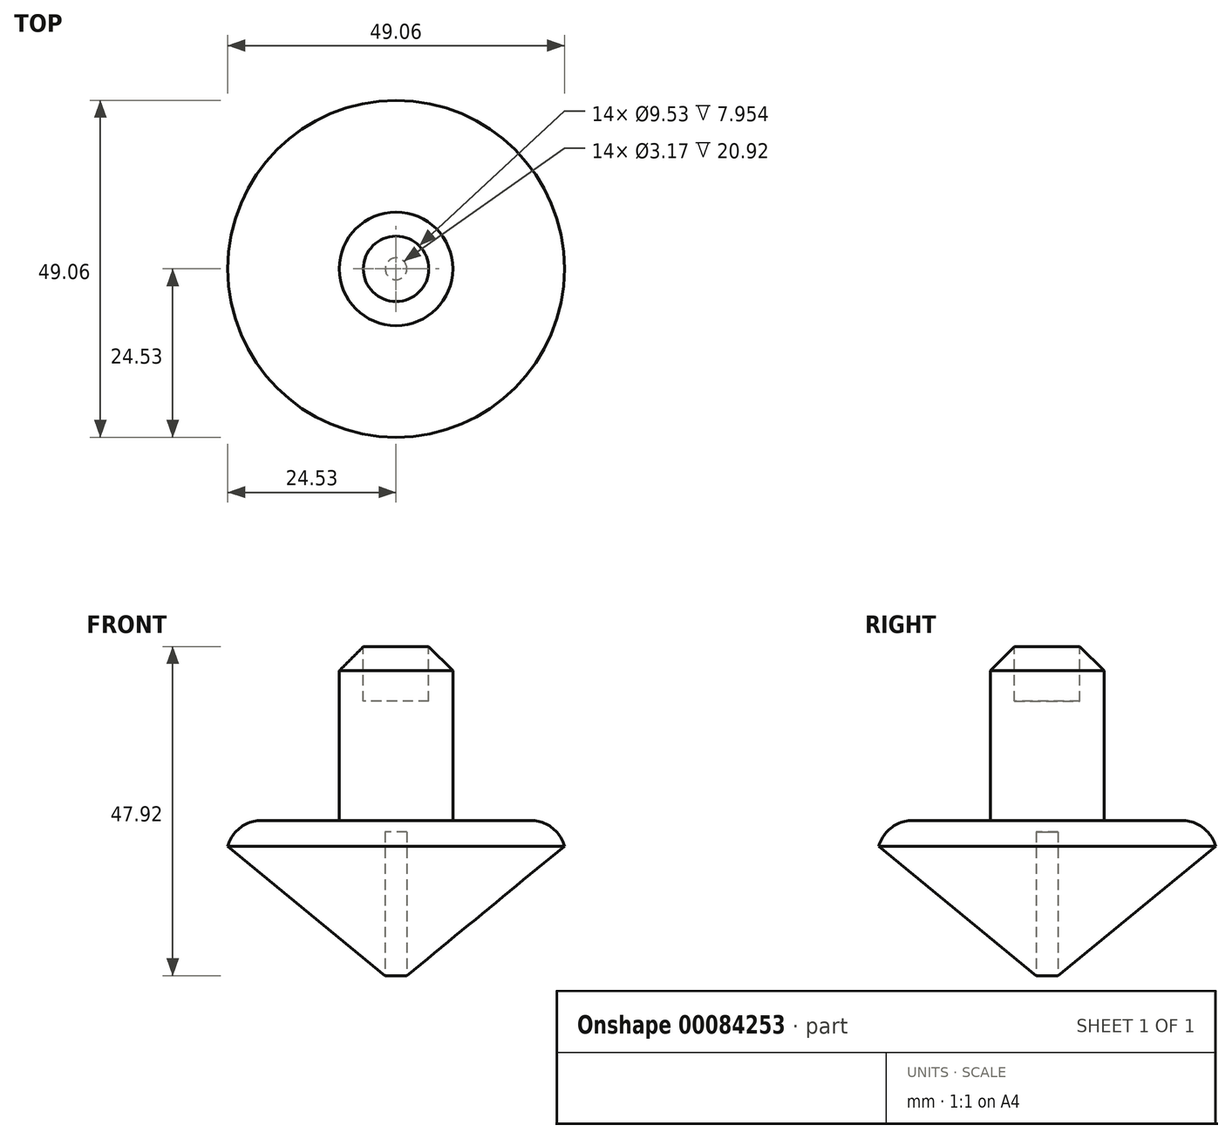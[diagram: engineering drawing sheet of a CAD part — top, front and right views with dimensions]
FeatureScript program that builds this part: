
annotation { "Feature Type Name" : "Feature", "Feature Type Description" : "" }
export const myFeature = defineFeature(function(context is Context, id is Id, definition is map)
    precondition{}
    {
        {
            var Q0;
            Q0=qCreatedBy(makeId("Front.planeOp"),FACE);
            var sketch = newSketch(context, id + "F0", { "sketchPlane" : qUnion([Q0])});
            skLineSegment(sketch, "E0", {"start": v(0, 0) * mm, "end": v(24.53, 20.16) * mm});
            skLineSegment(sketch, "E1", {"start": v(24.53, 20.16) * mm, "end": v(24.53, 23.9) * mm});
            skLineSegment(sketch, "E2", {"start": v(24.53, 23.9) * mm, "end": v(8.27, 23.9) * mm});
            skLineSegment(sketch, "E3", {"start": v(8.27, 23.9) * mm, "end": v(8.27, 50.8) * mm});
            skLineSegment(sketch, "E4", {"start": v(8.27, 50.8) * mm, "end": v(0, 50.8) * mm});
            skLineSegment(sketch, "E5", {"start": v(0, 50.8) * mm, "end": v(0, 0) * mm});
            skSolve(sketch);
        }
        {
            var Q0;
            Q0=qCreatedBy(makeId("Front.planeOp"),FACE);
            var sketch = newSketch(context, id + "F1", { "sketchPlane" : qUnion([Q0])});
            skSolve(sketch);
        }
        {
            var Q0;
            Q0 = qSketchRegion(id + "F1", true);
            var Q1;
            Q1=makeQuery(id+"F0.imprint","IMPRINT",FACE,{"disambiguationData":[TD([[makeQuery(id+"F0.imprint","IMPRINT",EDGE,{"derivedFrom":sQuery(id+"F0.wireOp",EDGE,"E0")}),1.0]])]});
            var Q2;
            Q2=sQuery(id+"F0.wireOp",EDGE,"E5");
            revolve(context, id + "F2", {"entities" : qUnion([Q0, Q1]), "axis" : qUnion([Q2]), "revolveType" : RevolveType.FULL});
        }
        {
            var Q0;
            Q0=makeQuery(id+"F2.opRevolve","SWEPT_EDGE",EDGE,{"disambiguationData":[OSD([sQuery(id+"F0.wireOp",EDGE,"E1"),sQuery(id+"F0.wireOp",EDGE,"E2")])]});
            fillet(context, id + "F3", {"entities" : qUnion([Q0]), "radius" : 5.08 * mm, "tangentPropagation" : true, "allowEdgeOverflow" : false});
        }
        {
            var Q0;
            Q0=makeQuery(id+"F2.opRevolve","SWEPT_FACE",FACE,{"disambiguationData":[OSD([sQuery(id+"F0.wireOp",EDGE,"E4")])]});
            var sketch = newSketch(context, id + "F4", { "sketchPlane" : qUnion([Q0])});
            skCircle(sketch, "E6", {"center": v(0, 0) * mm, "radius": 4.76 * mm});
            skSolve(sketch);
        }
        {
            var Q0;
            Q0=makeQuery(id+"F4.imprint","IMPRINT",FACE,{"disambiguationData":[TD([[makeQuery(id+"F4.imprint","IMPRINT",EDGE,{"derivedFrom":sQuery(id+"F4.wireOp",EDGE,"E6")}),1.0]])]});
            extrude(context, id + "F5", {"entities" : qUnion([Q0]), "operationType" : NewBodyOperationType.REMOVE, "oppositeDirection" : true, "depth" : 9.52 * mm});
        }
        {
            var Q0;
            Q0=makeQuery(id+"F2.opRevolve","SWEPT_EDGE",EDGE,{"disambiguationData":[OSD([sQuery(id+"F0.wireOp",EDGE,"E3"),sQuery(id+"F0.wireOp",EDGE,"E4")])]});
            chamfer(context, id + "F6", {"entities" : qUnion([Q0]), "width" : 5.08 * mm, "tangentPropagation" : true});
        }
        {
            var Q0;
            Q0=qCreatedBy(makeId("Top.planeOp"),FACE);
            var sketch = newSketch(context, id + "F7", { "sketchPlane" : qUnion([Q0])});
            skCircle(sketch, "E7", {"center": v(0, 0) * mm, "radius": 1.59 * mm});
            skSolve(sketch);
        }
        {
            var Q0;
            Q0 = qSketchRegion(id + "F7", true);
            extrude(context, id + "F8", {"entities" : qUnion([Q0]), "operationType" : NewBodyOperationType.REMOVE, "depth" : 22.22 * mm});
        }
    });
